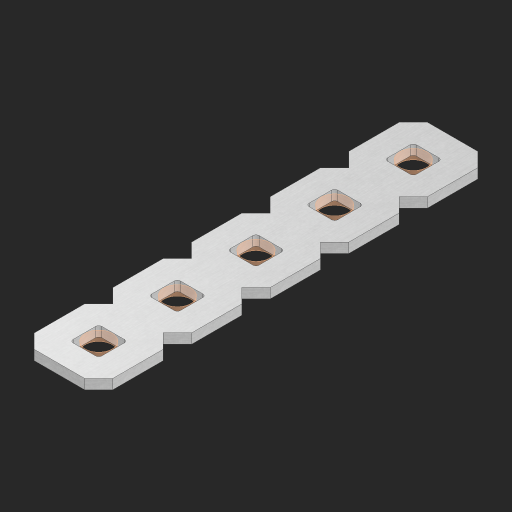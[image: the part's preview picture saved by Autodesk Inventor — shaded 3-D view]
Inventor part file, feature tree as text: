
AUTODESK INVENTOR PART (.ipt)
format: ipt  version: 2023 (Build 270158000, 158)  size: 322,560 bytes
history: native  units: in
note: dims shown in document units (in); Inventor stores cm internally (conversion verified against a paired STEP export)
features: other x6, extrude x4, sketch x2, pattern_linear x1
ambient origin geometry x8: Origin, YZ Plane, XZ Plane, XY Plane, X Axis, Y Axis, Z Axis, Center Point
bodies: Solid1 (feature_tree), Body (feature_tree)
feature tree (13):
  pattern_linear  "Rectangular Pattern1"  Spacing1=0.09in  [1 undecoded]
  sketch  "Sketch1"  dims[d1=0.5in]
  sketch  "Sketch2"  dims[d2=0.182in d3=0.09in d4=0.09in d5=0.09in d6=0.09in d7=0.09in d8=0.09in d9=0.09in d10=0.09in d11=0.02in d13=0.0in d14=0.172in d15=0.0625in d16=0.0in d19=0.5in d22=0.5in]
  other  "Srf1"
  other  "Srf126"
  other  "Srf127"
  other  "Srf128"
  other  "Srf129"
  other  "Circle"
  extrude  "ExtrusionSrf126"  Depth=0.09in
  extrude  "ExtrusionSrf127"  Depth=0.09in
  extrude  "ExtrusionSrf128"  Depth=0.09in
  extrude  "ExtrusionSrf129"  Depth=0.09in
note: 1 required parameter value undecoded (feature->parameter linkage not recoverable at this tier; creation-order binding heuristic only, values carry confidence <= 0.55)
